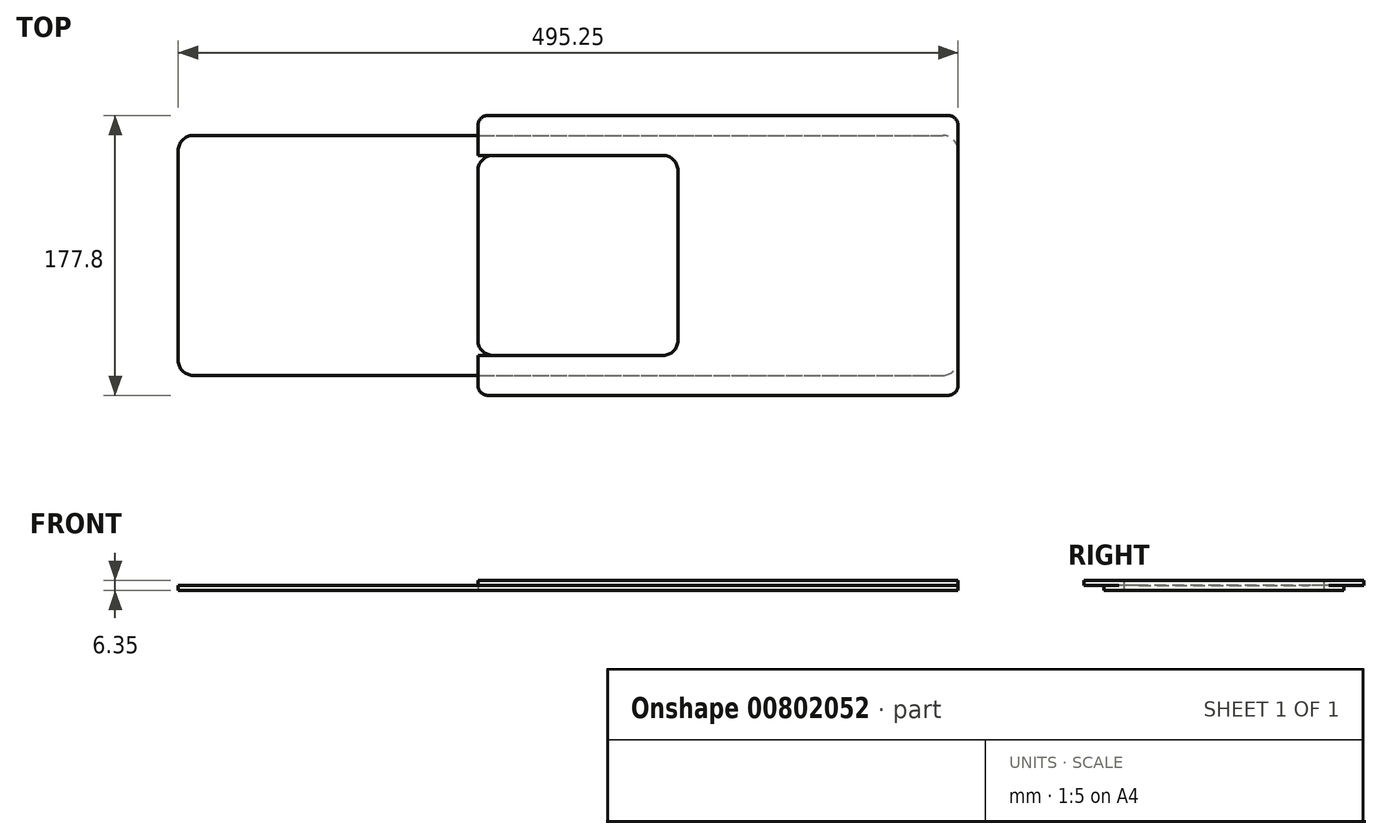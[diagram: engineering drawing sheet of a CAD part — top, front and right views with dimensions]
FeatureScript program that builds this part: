
annotation { "Feature Type Name" : "Feature", "Feature Type Description" : "" }
export const myFeature = defineFeature(function(context is Context, id is Id, definition is map)
    precondition{}
    {
        {
            var Q0;
            Q0=qCreatedBy(makeId("Top.planeOp"),FACE);
            var sketch = newSketch(context, id + "F0", { "sketchPlane" : qUnion([Q0])});
            skLineSegment(sketch, "E0.bottom", {"start": v(-9.53, 0) * mm, "end": v(-117.47, 0) * mm});
            skLineSegment(sketch, "E0.top", {"start": v(-9.53, 127) * mm, "end": v(-117.48, 127) * mm});
            skLineSegment(sketch, "E0.left", {"start": v(0, 9.53) * mm, "end": v(0, 117.47) * mm});
            skLineSegment(sketch, "E0.right", {"start": v(-127, 9.52) * mm, "end": v(-127, 117.47) * mm});
            skPoint(sketch, "E1.visualSharp", {"position": v(-127, 127) * mm});
            skArc(sketch, "E1.filletArc", {"start": v(-117.48, 127) * mm, "mid": v(-124.21, 124.21) * mm, "end": v(-127, 117.47) * mm});
            skPoint(sketch, "E2.visualSharp", {"position": v(0, 127) * mm});
            skArc(sketch, "E2.filletArc", {"start": v(0, 117.47) * mm, "mid": v(-2.79, 124.21) * mm, "end": v(-9.53, 127) * mm});
            skPoint(sketch, "E3.visualSharp", {"position": v(0, 0) * mm});
            skArc(sketch, "E3.filletArc", {"start": v(-9.52, 0) * mm, "mid": v(-2.79, 2.79) * mm, "end": v(0, 9.53) * mm});
            skPoint(sketch, "E4.visualSharp", {"position": v(-127, 0) * mm});
            skArc(sketch, "E4.filletArc", {"start": v(-127, 9.53) * mm, "mid": v(-124.21, 2.79) * mm, "end": v(-117.47, 0) * mm});
            skLineSegment(sketch, "E5.bottom", {"start": v(-307.82, 139.7) * mm, "end": v(168.37, 139.7) * mm});
            skLineSegment(sketch, "E5.top", {"start": v(-307.82, -12.7) * mm, "end": v(168.37, -12.7) * mm});
            skLineSegment(sketch, "E5.left", {"start": v(-317.35, 130.17) * mm, "end": v(-317.35, -3.18) * mm});
            skLineSegment(sketch, "E5.right", {"start": v(177.9, 130.18) * mm, "end": v(177.9, -3.17) * mm});
            skPoint(sketch, "E6.visualSharp", {"position": v(-317.35, 139.7) * mm});
            skArc(sketch, "E6.filletArc", {"start": v(-307.82, 139.7) * mm, "mid": v(-314.56, 136.91) * mm, "end": v(-317.35, 130.17) * mm});
            skPoint(sketch, "E7.visualSharp", {"position": v(177.9, 139.7) * mm});
            skArc(sketch, "E7.filletArc", {"start": v(177.9, 130.18) * mm, "mid": v(175.1, 136.91) * mm, "end": v(168.37, 139.7) * mm});
            skPoint(sketch, "E8.visualSharp", {"position": v(177.9, -12.7) * mm});
            skArc(sketch, "E8.filletArc", {"start": v(168.37, -12.7) * mm, "mid": v(175.1, -9.91) * mm, "end": v(177.9, -3.17) * mm});
            skPoint(sketch, "E9.visualSharp", {"position": v(-317.35, -12.7) * mm});
            skArc(sketch, "E9.filletArc", {"start": v(-317.35, -3.18) * mm, "mid": v(-314.56, -9.91) * mm, "end": v(-307.82, -12.7) * mm});
            skSolve(sketch);
        }
        {
            var Q0;
            Q0=qSketchRegion(id+"F0",true);
            extrude(context, id + "F1", {"entities" : qUnion([Q0]), "depth" : 3.17 * mm});
        }
        {
            var Q0;
            Q0=makeQuery(id+"F1.opExtrude","CAP_FACE",FACE,{"disambiguationData":[OSD([sQuery(id+"F0.wireOp",EDGE,"E0.bottom"),sQuery(id+"F0.wireOp",EDGE,"E0.top"),sQuery(id+"F0.wireOp",EDGE,"E0.left"),sQuery(id+"F0.wireOp",EDGE,"E0.right"),sQuery(id+"F0.wireOp",EDGE,"E1.filletArc"),sQuery(id+"F0.wireOp",EDGE,"E2.filletArc"),sQuery(id+"F0.wireOp",EDGE,"E3.filletArc"),sQuery(id+"F0.wireOp",EDGE,"E4.filletArc"),sQuery(id+"F0.wireOp",EDGE,"E5.bottom"),sQuery(id+"F0.wireOp",EDGE,"E5.top"),sQuery(id+"F0.wireOp",EDGE,"E5.left"),sQuery(id+"F0.wireOp",EDGE,"E5.right"),sQuery(id+"F0.wireOp",EDGE,"E6.filletArc"),sQuery(id+"F0.wireOp",EDGE,"E7.filletArc"),sQuery(id+"F0.wireOp",EDGE,"E8.filletArc"),sQuery(id+"F0.wireOp",EDGE,"E9.filletArc")])],"isStart":false});
            var sketch = newSketch(context, id + "F2", { "sketchPlane" : qUnion([Q0])});
            skLineSegment(sketch, "E10.bottom", {"start": v(-120.65, 152.4) * mm, "end": v(171.55, 152.4) * mm});
            skLineSegment(sketch, "E10.top", {"start": v(-120.65, -25.4) * mm, "end": v(171.55, -25.4) * mm});
            skLineSegment(sketch, "E10.left", {"start": v(-127, 146.05) * mm, "end": v(-127, 127) * mm});
            skLineSegment(sketch, "E10.right", {"start": v(177.9, 146.05) * mm, "end": v(177.9, -19.05) * mm});
            skLineSegment(sketch, "E11.bottom", {"start": v(-127, 127) * mm, "end": v(-9.52, 127) * mm});
            skLineSegment(sketch, "E11.top", {"start": v(-127, 0) * mm, "end": v(-9.53, 0) * mm});
            skLineSegment(sketch, "E11.right", {"start": v(0, 117.47) * mm, "end": v(0, 9.53) * mm});
            skLineSegment(sketch, "E12.trimOffspring", {"start": v(-127, 0) * mm, "end": v(-127, -19.05) * mm});
            skPoint(sketch, "E13.visualSharp", {"position": v(0, 127) * mm});
            skArc(sketch, "E13.filletArc", {"start": v(0, 117.47) * mm, "mid": v(-2.79, 124.21) * mm, "end": v(-9.52, 127) * mm});
            skPoint(sketch, "E14.visualSharp", {"position": v(0, 0) * mm});
            skArc(sketch, "E14.filletArc", {"start": v(-9.53, 0) * mm, "mid": v(-2.79, 2.79) * mm, "end": v(0, 9.53) * mm});
            skPoint(sketch, "E15.visualSharp", {"position": v(-127, 152.4) * mm});
            skArc(sketch, "E15.filletArc", {"start": v(-120.65, 152.4) * mm, "mid": v(-125.14, 150.54) * mm, "end": v(-127, 146.05) * mm});
            skPoint(sketch, "E16.visualSharp", {"position": v(-127, -25.4) * mm});
            skArc(sketch, "E16.filletArc", {"start": v(-127, -19.05) * mm, "mid": v(-125.14, -23.54) * mm, "end": v(-120.65, -25.4) * mm});
            skPoint(sketch, "E17.visualSharp", {"position": v(177.9, -25.4) * mm});
            skArc(sketch, "E17.filletArc", {"start": v(171.55, -25.4) * mm, "mid": v(176.04, -23.54) * mm, "end": v(177.9, -19.05) * mm});
            skPoint(sketch, "E18.visualSharp", {"position": v(177.9, 152.4) * mm});
            skArc(sketch, "E18.filletArc", {"start": v(177.9, 146.05) * mm, "mid": v(176.04, 150.54) * mm, "end": v(171.55, 152.4) * mm});
            skSolve(sketch);
        }
        {
            var Q0;
            Q0=qSketchRegion(id+"F2",true);
            extrude(context, id + "F3", {"entities" : qUnion([Q0]), "operationType" : NewBodyOperationType.ADD, "depth" : 3.17 * mm, "offsetDistance" : 25 * mm});
        }
    });
